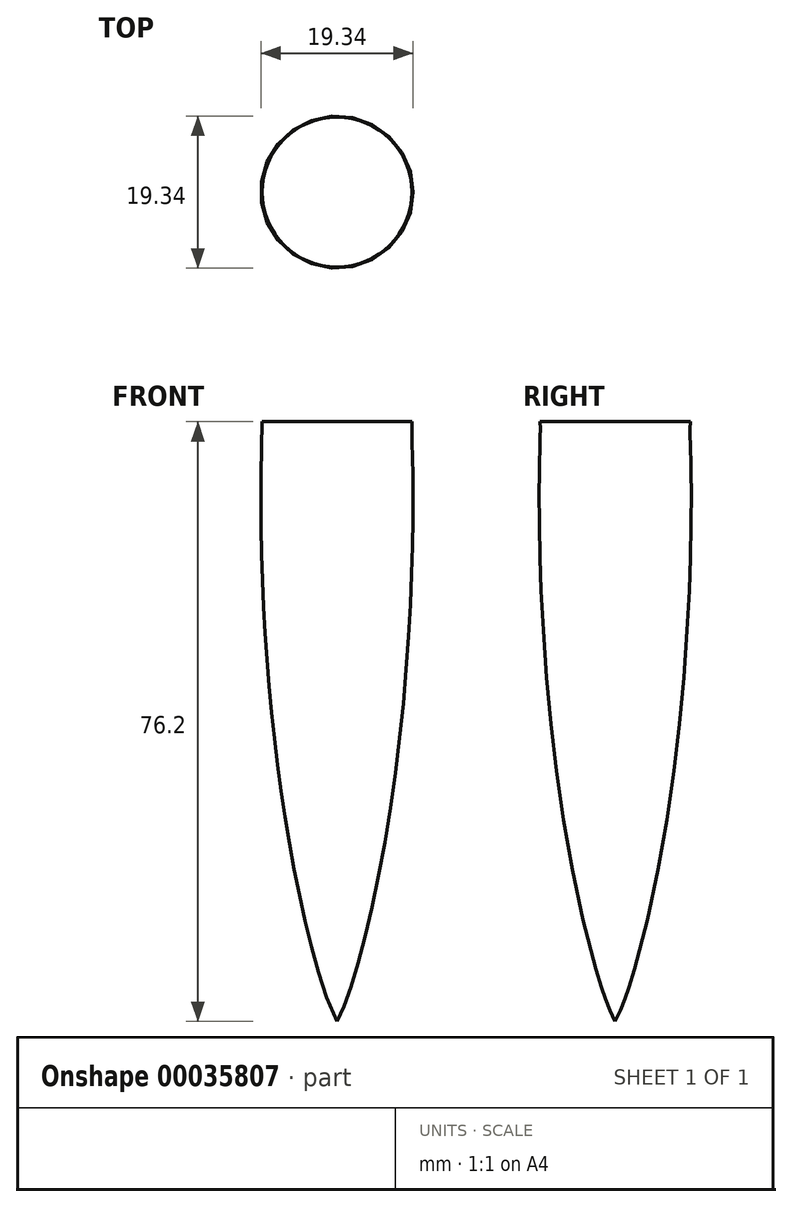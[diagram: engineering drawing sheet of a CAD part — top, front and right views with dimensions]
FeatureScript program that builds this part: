
annotation { "Feature Type Name" : "Feature", "Feature Type Description" : "" }
export const myFeature = defineFeature(function(context is Context, id is Id, definition is map)
    precondition{}
    {
        {
            var Q0;
            Q0=qCreatedBy(makeId("Front.planeOp"),FACE);
            var sketch = newSketch(context, id + "F0", { "sketchPlane" : qUnion([Q0])});
            skFitSpline(sketch, "E0", {"points": [v(0, 0) * mm, v(7.4, 31.4) * mm, v(9.66, 68.25) * mm, v(9.53, 76.2) * mm], "startDerivative": vector(19.85, 37.37) * mm, "endDerivative": vector(0.97, 22.42) * mm});
            skLineSegment(sketch, "E1", {"start": v(9.52, 76.2) * mm, "end": v(0, 76.2) * mm});
            skLineSegment(sketch, "E2", {"start": v(0, 76.2) * mm, "end": v(0, 0) * mm});
            skSolve(sketch);
        }
        {
            var Q0;
            Q0=makeQuery(id+"F0.imprint","IMPRINT",FACE,{"disambiguationData":[TD([[makeQuery(id+"F0.imprint","IMPRINT",EDGE,{"derivedFrom":sQuery(id+"F0.wireOp",EDGE,"E0")}),1.0]])]});
            var Q1;
            Q1=sQuery(id+"F0.wireOp",EDGE,"E2");
            revolve(context, id + "F1", {"entities" : qUnion([Q0]), "axis" : qUnion([Q1]), "revolveType" : RevolveType.FULL});
        }
    });
